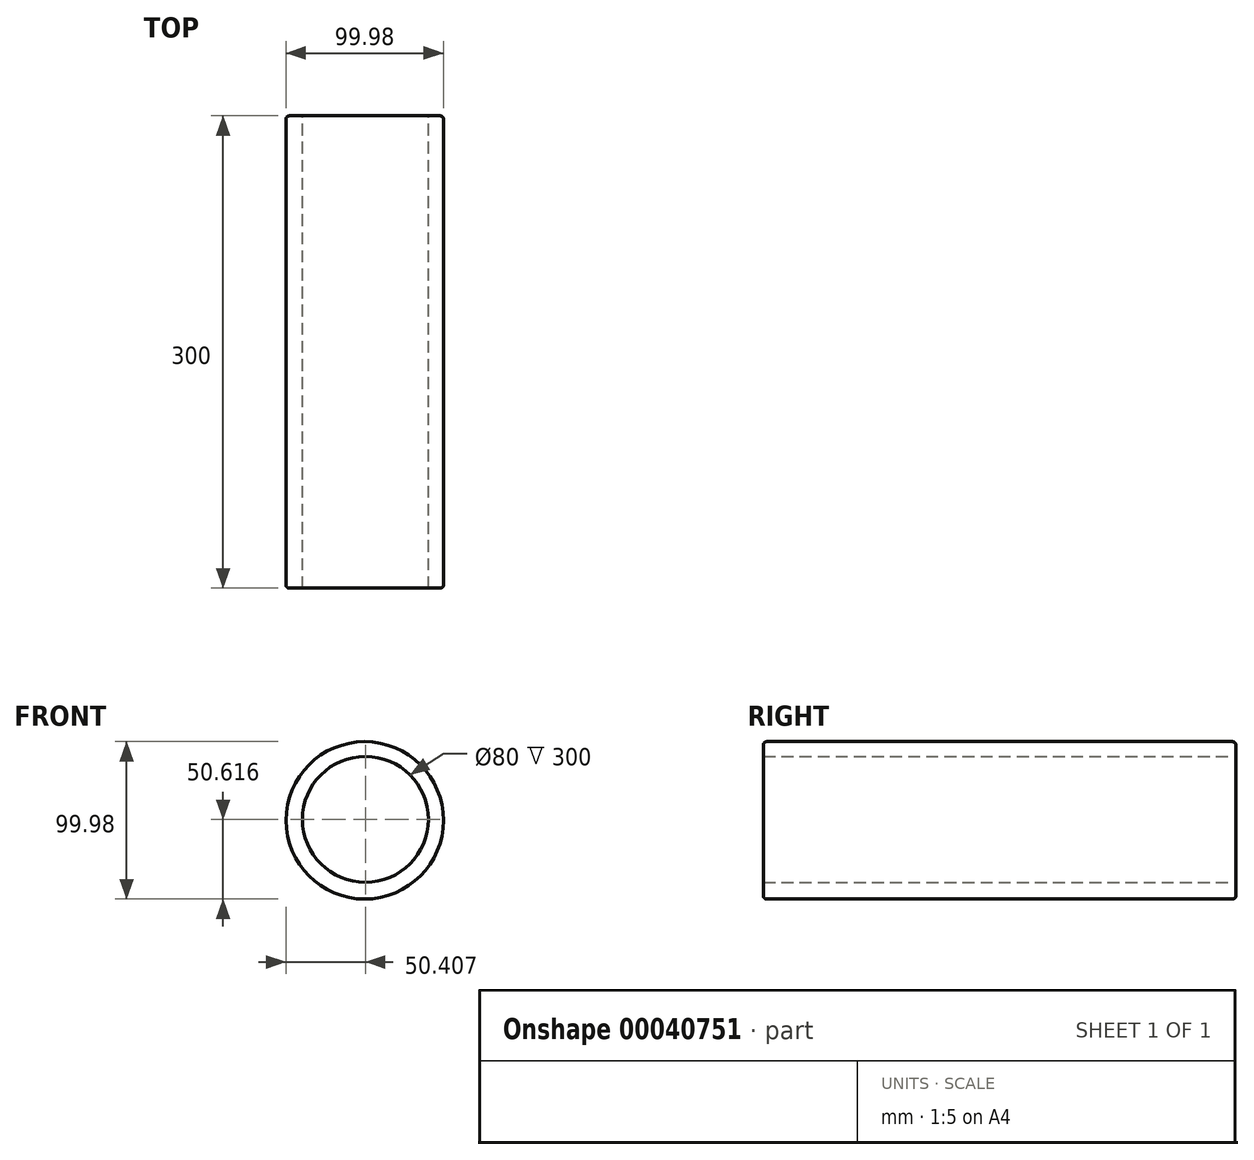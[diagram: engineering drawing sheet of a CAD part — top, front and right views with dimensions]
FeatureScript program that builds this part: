
annotation { "Feature Type Name" : "Feature", "Feature Type Description" : "" }
export const myFeature = defineFeature(function(context is Context, id is Id, definition is map)
    precondition{}
    {
        {
            var Q0;
            Q0=qCreatedBy(makeId("Front.planeOp"),FACE);
            var sketch = newSketch(context, id + "F0", { "sketchPlane" : qUnion([Q0])});
            skCircle(sketch, "E0", {"center": v(0, 0) * mm, "radius": 50 * mm});
            skCircle(sketch, "E1", {"center": v(0.42, 0.63) * mm, "radius": 40 * mm});
            skSolve(sketch);
        }
        {
            var Q0;
            Q0=makeQuery(id+"F0.imprint","IMPRINT",FACE,{"disambiguationData":[TD([[makeQuery(id+"F0.imprint","IMPRINT",EDGE,{"derivedFrom":sQuery(id+"F0.wireOp",EDGE,"E0")}),1.0]])]});
            extrude(context, id + "F1", {"entities" : qUnion([Q0]), "depth" : 300 * mm, "symmetric" : true});
        }
        {
            var Q0;
            Q0=makeQuery(id+"F1.opExtrude","CAP_EDGE",EDGE,{"disambiguationData":[OSD([sQuery(id+"F0.wireOp",EDGE,"E0")])],"isStart":false});
            var Q1;
            Q1=makeQuery(id+"F1.opExtrude","CAP_EDGE",EDGE,{"disambiguationData":[OSD([sQuery(id+"F0.wireOp",EDGE,"E0")])],"isStart":true});
            fillet(context, id + "F2", {"entities" : qUnion([Q0, Q1]), "radius" : 2 * mm, "tangentPropagation" : true, "allowEdgeOverflow" : false});
        }
    });
